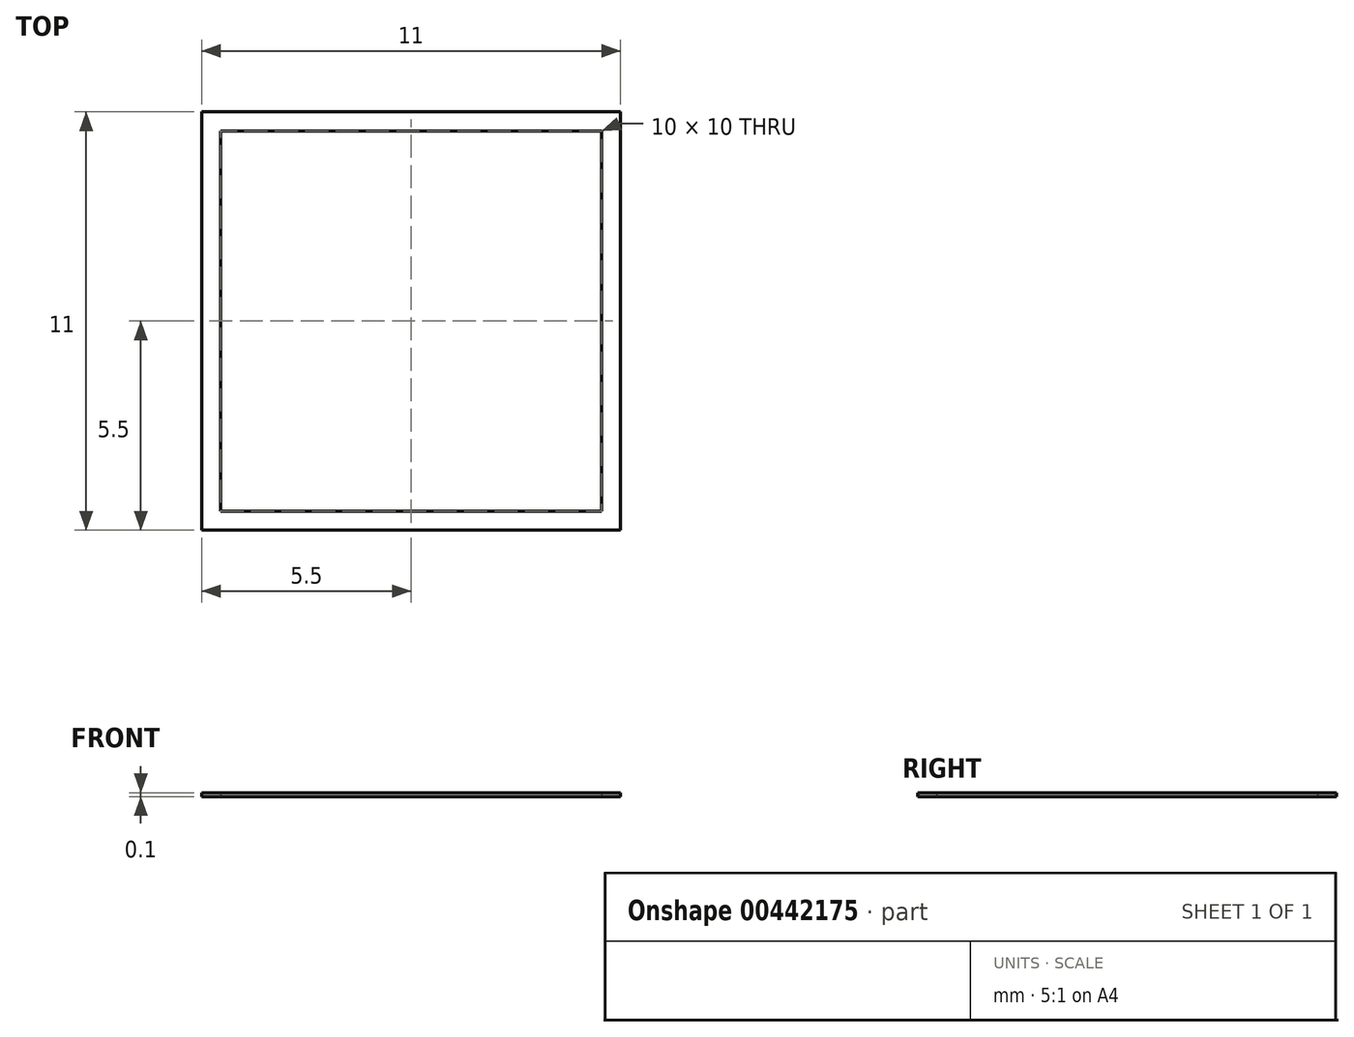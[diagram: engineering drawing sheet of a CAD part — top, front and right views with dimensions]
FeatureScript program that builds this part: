
annotation { "Feature Type Name" : "Feature", "Feature Type Description" : "" }
export const myFeature = defineFeature(function(context is Context, id is Id, definition is map)
    precondition{}
    {
        {
            var Q0;
            Q0=qCreatedBy(makeId("Top.planeOp"),FACE);
            var sketch = newSketch(context, id + "F0", { "sketchPlane" : qUnion([Q0])});
            skLineSegment(sketch, "E0.bottom", {"start": v(-5, 5) * mm, "end": v(5, 5) * mm});
            skLineSegment(sketch, "E0.top", {"start": v(-5, -5) * mm, "end": v(5, -5) * mm});
            skLineSegment(sketch, "E0.left", {"start": v(-5, 5) * mm, "end": v(-5, -5) * mm});
            skLineSegment(sketch, "E0.right", {"start": v(5, 5) * mm, "end": v(5, -5) * mm});
            skPoint(sketch, "E0.middle", {"position": v(0, 0) * mm});
            skLineSegment(sketch, "E1.bottom", {"start": v(-5.5, 5.5) * mm, "end": v(5.5, 5.5) * mm});
            skLineSegment(sketch, "E1.top", {"start": v(-5.5, -5.5) * mm, "end": v(5.5, -5.5) * mm});
            skLineSegment(sketch, "E1.left", {"start": v(-5.5, 5.5) * mm, "end": v(-5.5, -5.5) * mm});
            skLineSegment(sketch, "E1.right", {"start": v(5.5, 5.5) * mm, "end": v(5.5, -5.5) * mm});
            skSolve(sketch);
        }
        {
            var Q0;
            Q0=makeQuery(id+"F0.imprint","IMPRINT",FACE,{"disambiguationData":[TD([[makeQuery(id+"F0.imprint","IMPRINT",EDGE,{"derivedFrom":sQuery(id+"F0.wireOp",EDGE,"E0.bottom")}),1.0]])]});
            extrude(context, id + "F1", {"entities" : qUnion([Q0]), "depth" : 0.1 * mm});
        }
    });
